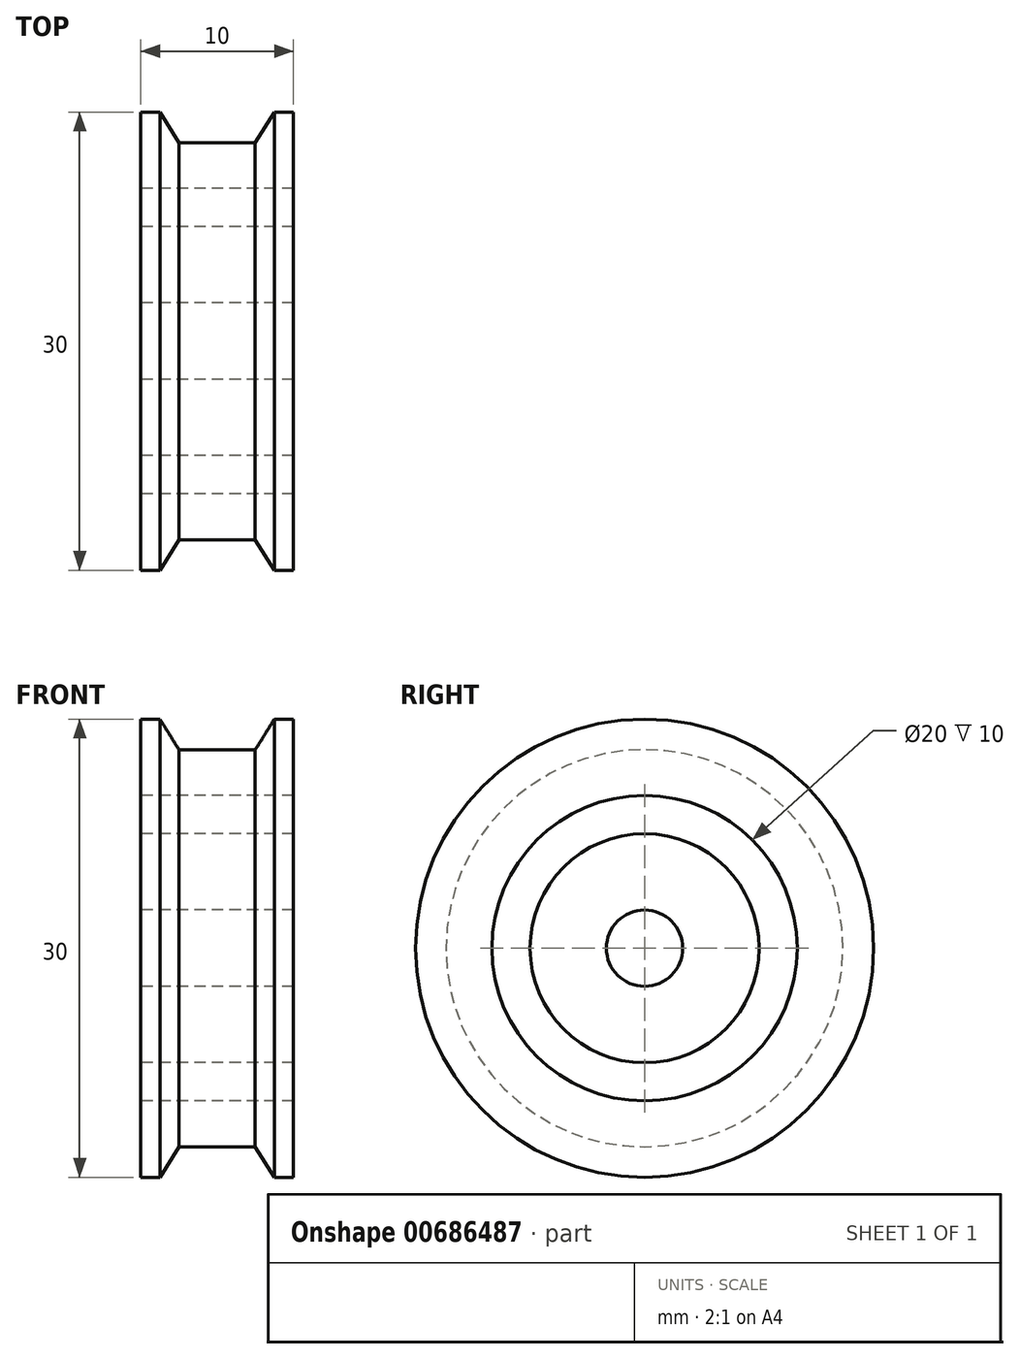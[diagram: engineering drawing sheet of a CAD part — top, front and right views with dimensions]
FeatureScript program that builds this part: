
annotation { "Feature Type Name" : "Feature", "Feature Type Description" : "" }
export const myFeature = defineFeature(function(context is Context, id is Id, definition is map)
    precondition{}
    {
        {
            var Q0;
            Q0=qCreatedBy(makeId("Front.planeOp"),FACE);
            var sketch = newSketch(context, id + "F0", { "sketchPlane" : qUnion([Q0])});
            skLineSegment(sketch, "E0.bottom", {"start": v(-5, 0) * mm, "end": v(5, 0) * mm});
            skLineSegment(sketch, "E0.top", {"start": v(-5, 5) * mm, "end": v(5, 5) * mm});
            skLineSegment(sketch, "E0.left", {"start": v(-5, 0) * mm, "end": v(-5, 5) * mm});
            skLineSegment(sketch, "E0.right", {"start": v(5, 0) * mm, "end": v(5, 5) * mm});
            skLineSegment(sketch, "E1.bottom", {"start": v(-2.5, 5) * mm, "end": v(2.5, 5) * mm});
            skLineSegment(sketch, "E1.top", {"start": v(-2.5, 7.5) * mm, "end": v(2.5, 7.5) * mm});
            skLineSegment(sketch, "E2.bottom", {"start": v(-5, 7.5) * mm, "end": v(5, 7.5) * mm});
            skLineSegment(sketch, "E2.left", {"start": v(-5, 7.5) * mm, "end": v(-5, 12.5) * mm});
            skLineSegment(sketch, "E2.right", {"start": v(5, 7.5) * mm, "end": v(5, 12.5) * mm});
            skLineSegment(sketch, "E3", {"start": v(-7.9, -2.5) * mm, "end": v(9.1, -2.5) * mm});
            skLineSegment(sketch, "E4.top", {"start": v(-2.5, 10.5) * mm, "end": v(2.5, 10.5) * mm});
            skLineSegment(sketch, "E5", {"start": v(-5, 12.5) * mm, "end": v(-3.75, 12.5) * mm});
            skLineSegment(sketch, "E6", {"start": v(-3.75, 12.5) * mm, "end": v(-2.5, 10.5) * mm});
            skLineSegment(sketch, "E7", {"start": v(5, 12.5) * mm, "end": v(3.75, 12.5) * mm});
            skLineSegment(sketch, "E8", {"start": v(3.75, 12.5) * mm, "end": v(2.5, 10.5) * mm});
            skLineSegment(sketch, "E9", {"start": v(-5, 7.5) * mm, "end": v(-5, 5) * mm});
            skLineSegment(sketch, "E10", {"start": v(5, 7.5) * mm, "end": v(5, 5) * mm});
            skSolve(sketch);
        }
        {
            var Q0;
            {var subQ0=sQuery(id+"F0.wireOp",EDGE,"E2.left");Q0=makeQuery(id+"F0.imprint","IMPRINT",FACE,{"disambiguationData":[TD([[makeQuery(id+"F0.imprint","IMPRINT",EDGE,{"derivedFrom":subQ0}),-1.0]])]});}
            var Q1;
            Q1=makeQuery(id+"F0.imprint","IMPRINT",FACE,{"disambiguationData":[TD([[makeQuery(id+"F0.imprint","IMPRINT",EDGE,{"derivedFrom":sQuery(id+"F0.wireOp",EDGE,"E1.bottom")}),1.0]])]});
            var Q2;
            Q2=makeQuery(id+"F0.imprint","IMPRINT",FACE,{"disambiguationData":[TD([[makeQuery(id+"F0.imprint","IMPRINT",EDGE,{"derivedFrom":sQuery(id+"F0.wireOp",EDGE,"E0.bottom")}),1.0]])]});
            var Q3;
            Q3=sQuery(id+"F0.wireOp",EDGE,"E3");
            revolve(context, id + "F1", {"entities" : qUnion([Q0, Q1, Q2]), "axis" : qUnion([Q3]), "revolveType" : RevolveType.FULL});
        }
    });
